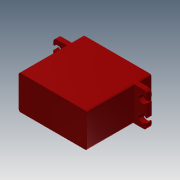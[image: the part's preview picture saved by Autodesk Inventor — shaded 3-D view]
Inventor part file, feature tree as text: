
AUTODESK INVENTOR PART (.ipt)
format: ipt  version: 2015 (Build 190159000, 159)  size: 213,504 bytes
history: native  units: mm
features: fillet x12, extrude x8, sketch x8, chamfer x1
ambient origin geometry x8: Origin, YZ Plane, XZ Plane, XY Plane, X Axis, Y Axis, Z Axis, Center Point
bodies: Solid1 (feature_tree)
feature tree (29):
  extrude  "Extrusion1"  Depth=7.4mm TaperAngle=0.0deg
  sketch  "Sketch2"  dims[d10=7.4mm d11=0.0mm d18=5.8mm d19=0.0mm]
  extrude  "Extrusion2"  Depth=5.8mm TaperAngle=0.0deg
  extrude  "Extrusion3"  Depth=4.0mm TaperAngle=0.0deg
  extrude  "Extrusion4"  Depth=2.0mm
  extrude  "Extrusion5"  Depth=2.0mm
  fillet  "Fillet1"  Radius=1.0mm
  fillet  "Fillet2"  Radius=1.0mm
  fillet  "Fillet3"  Radius=1.0mm
  fillet  "Fillet4"  Radius=1.0mm
  fillet  "Fillet5"  Radius=1.0mm
  fillet  "Fillet6"  Radius=1.0mm
  fillet  "Fillet7"  Radius=1.0mm
  fillet  "Fillet8"  Radius=1.0mm
  fillet  "Fillet9"  Radius=4.0mm
  fillet  "Fillet10"  Radius=3.0mm
  fillet  "Fillet11"  Radius=3.0mm
  fillet  "Fillet12"  [1 undecoded]
  extrude  "Extrusion6"  [1 undecoded]
  chamfer  "Chamfer3"  [1 undecoded]
  sketch  "Sketch7"
  sketch  "Sketch8"
  extrude  "Extrusion7"  [1 undecoded]
  extrude  "Extrusion8"  [1 undecoded]
  sketch  "Sketch1"  dims[d2=43.7mm d3=0.0mm d8=7.4mm d9=0.0mm]
  sketch  "Sketch3"  dims[d20=5.0mm d21=4.0mm d22=0.0mm]
  sketch  "Sketch4"  dims[d26=2.0mm d27=2.0mm]
  sketch  "Sketch5"  dims[d28=2.0mm d29=2.0mm d30=1.0mm d31=1.0mm d32=1.0mm d33=1.0mm d34=1.0mm d35=1.0mm d36=1.0mm d37=1.0mm d39=4.0mm d40=0.0mm]
  sketch  "Sketch6"  dims[d44=1.8mm d45=1.6mm d46=45.0deg d71=3.0mm d72=0.0mm d73=3.0mm d74=0.0mm]
note: 5 required parameter values undecoded (feature->parameter linkage not recoverable at this tier; creation-order binding heuristic only, values carry confidence <= 0.55)
